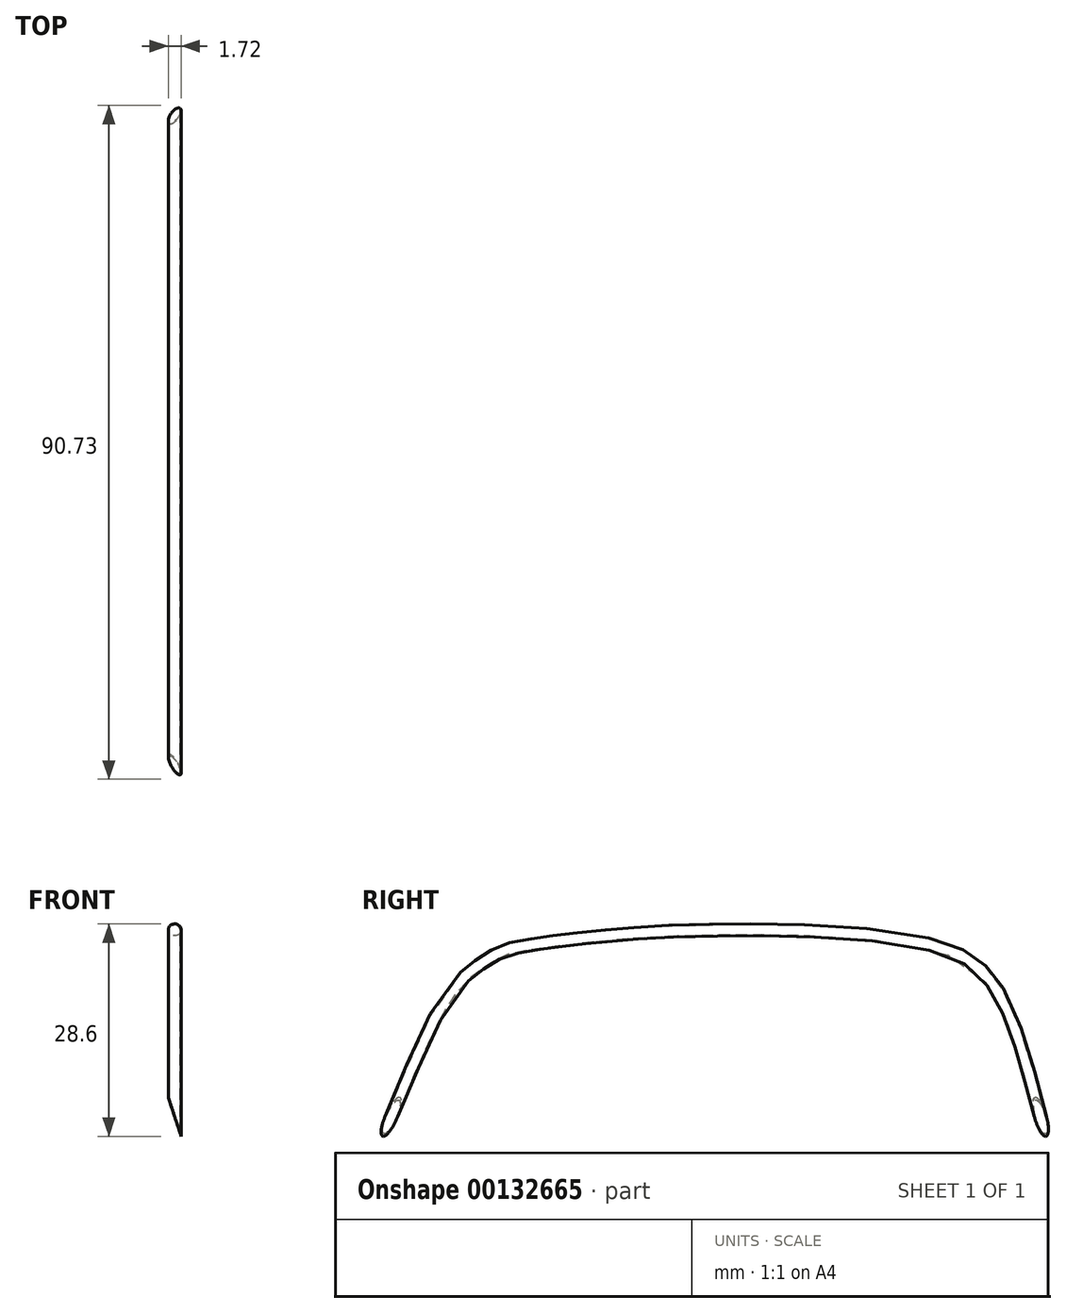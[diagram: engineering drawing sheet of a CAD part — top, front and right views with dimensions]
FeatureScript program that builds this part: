
annotation { "Feature Type Name" : "Feature", "Feature Type Description" : "" }
export const myFeature = defineFeature(function(context is Context, id is Id, definition is map)
    precondition{}
    {
        {
            var Q0;
            Q0=qCreatedBy(makeId("Right.planeOp"),FACE);
            var sketch = newSketch(context, id + "F0", { "sketchPlane" : qUnion([Q0])});
            skFitSpline(sketch, "E0", {"points": [v(-62.32, -10.16) * mm, v(-55.93, 4.66) * mm, v(-51.43, 11.36) * mm, v(-47.24, 14.3) * mm, v(-46.34, 14.76) * mm, v(-45.36, 15.13) * mm, v(-30.8, 17.02) * mm, v(-16.77, 17.64) * mm, v(-2.42, 17.43) * mm, v(11.92, 15.55) * mm, v(18, 12.51) * mm, v(21.98, 6.33) * mm, v(26.06, -7.07) * mm, v(30.35, -23.62) * mm], "startDerivative": vector(65.13, 158.51) * mm, "endDerivative": vector(41.25, -159.34) * mm});
            skSolve(sketch);
        }
        {
            var Q0;
            Q0=qCreatedBy(makeId("Top.planeOp"),FACE);
            cPlane(context, id + "F1", {"entities" : qUnion([Q0]), "cplaneType" : CPlaneType.OFFSET, "offset" : 10.16 * mm, "oppositeDirection" : true, "width" : 152.4 * mm, "height" : 152.4 * mm});
        }
        {
            var Q0;
            Q0=qCreatedBy(id+"F1.planeOp",FACE);
            var sketch = newSketch(context, id + "F2", { "sketchPlane" : qUnion([Q0])});
            skCircle(sketch, "E1", {"center": v(0, -62.32) * mm, "radius": 0.86 * mm});
            skCircle(sketch, "E2", {"center": v(0, -62.32) * mm, "radius": 0.75 * mm});
            skSolve(sketch);
        }
        {
            var Q0;
            Q0=makeQuery(id+"F2.imprint","IMPRINT",FACE,{"disambiguationData":[TD([[makeQuery(id+"F2.imprint","IMPRINT",EDGE,{"derivedFrom":sQuery(id+"F2.wireOp",EDGE,"E1")}),1.0]])]});
            var Q1;
            Q1=sQuery(id+"F0.wireOp",EDGE,"E0");
            sweep(context, id + "F3", {"profiles" : qUnion([Q0]), "path" : qUnion([Q1])});
        }
        {
            var Q0;
            Q0=qCreatedBy(makeId("Front.planeOp"),FACE);
            var sketch = newSketch(context, id + "F4", { "sketchPlane" : qUnion([Q0])});
            skLineSegment(sketch, "E3", {"start": v(5.94, -25.6) * mm, "end": v(-2.15, -0.94) * mm});
            skLineSegment(sketch, "E4", {"start": v(5.94, -25.6) * mm, "end": v(-2.25, -25.6) * mm});
            skLineSegment(sketch, "E5", {"start": v(-2.25, -25.6) * mm, "end": v(-2.15, -0.94) * mm});
            skSolve(sketch);
        }
        {
            var Q0;
            Q0 = qSketchRegion(id + "F4", true);
            extrude(context, id + "F5", {"entities" : qUnion([Q0]), "operationType" : NewBodyOperationType.REMOVE, "endBound" : BoundingType.THROUGH_ALL, "depth" : 79.02 * mm, "hasSecondDirection" : true, "secondDirectionBound" : SecondDirectionBoundingType.THROUGH_ALL, "secondDirectionOppositeDirection" : true, "secondDirectionDepth" : 25.4 * mm});
        }
    });
